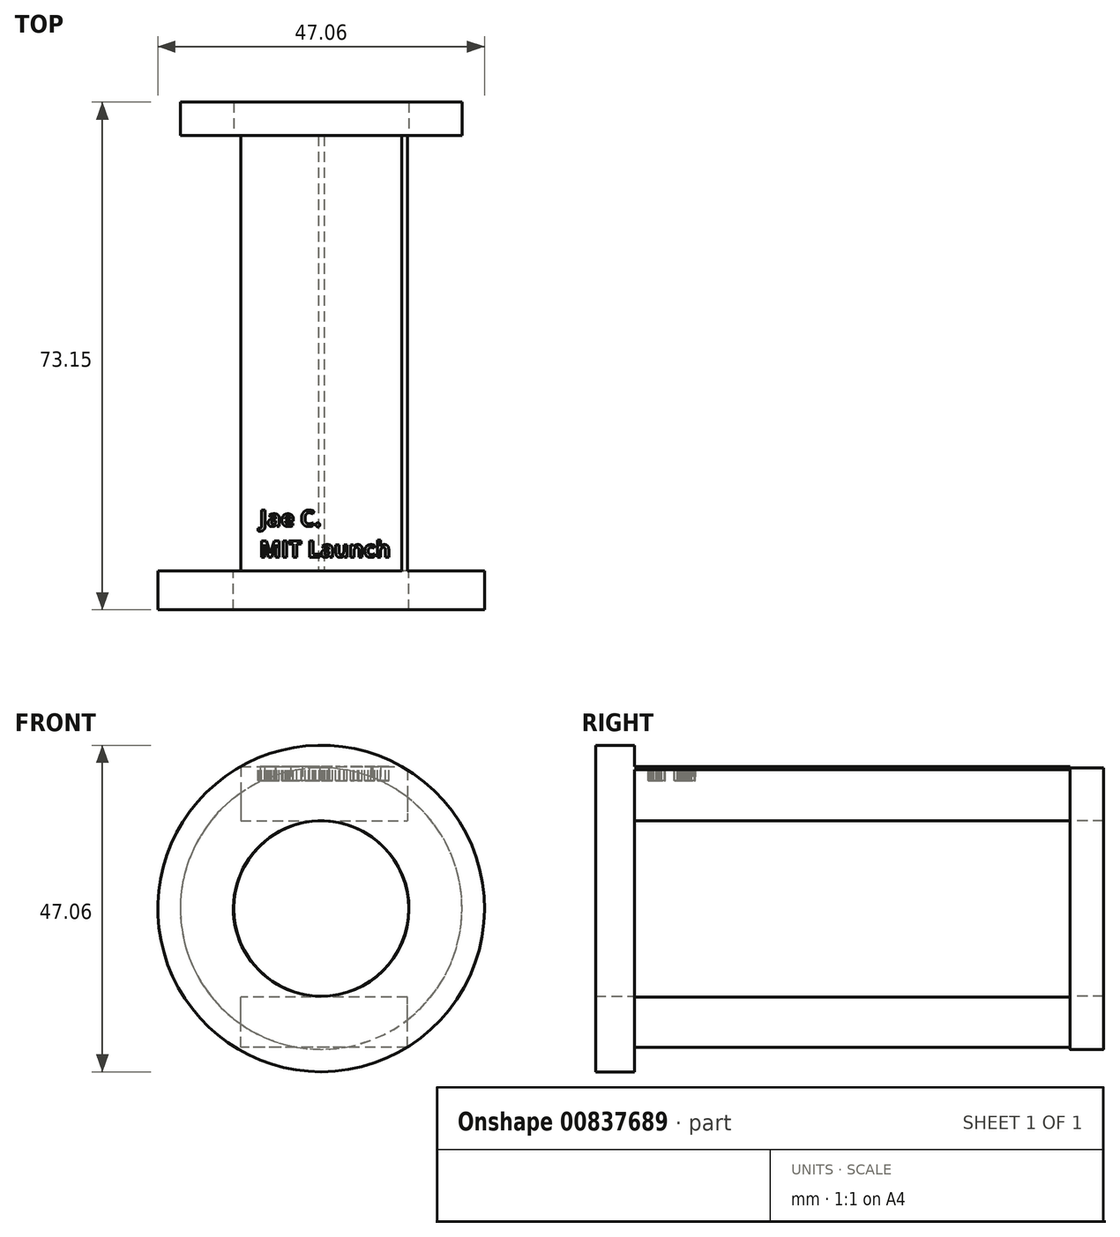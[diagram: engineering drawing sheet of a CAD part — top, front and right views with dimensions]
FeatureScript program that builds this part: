
annotation { "Feature Type Name" : "Feature", "Feature Type Description" : "" }
export const myFeature = defineFeature(function(context is Context, id is Id, definition is map)
    precondition{}
    {
        {
            var Q0;
            Q0=qCreatedBy(makeId("Front.planeOp"),FACE);
            var sketch = newSketch(context, id + "F0", { "sketchPlane" : qUnion([Q0])});
            skCircle(sketch, "E0", {"center": v(0, 0) * mm, "radius": 12.65 * mm});
            skCircle(sketch, "E1", {"center": v(0, 0) * mm, "radius": 23.53 * mm});
            skSolve(sketch);
        }
        {
            var Q0;
            Q0 = qSketchRegion(id + "F0", true);
            extrude(context, id + "F1", {"entities" : qUnion([Q0]), "depth" : 5.6 * mm, "offsetDistance" : 25.4 * mm});
        }
        {
            var Q0;
            Q0=makeQuery(id+"F1.opExtrude","CAP_FACE",FACE,{"disambiguationData":[OSD([sQuery(id+"F0.wireOp",EDGE,"E0"),sQuery(id+"F0.wireOp",EDGE,"E1")])],"isStart":true});
            var sketch = newSketch(context, id + "F2", { "sketchPlane" : qUnion([Q0])});
            skLineSegment(sketch, "E2.bottom", {"start": v(11.6, 20.47) * mm, "end": v(-12.41, 20.47) * mm});
            skLineSegment(sketch, "E2.top", {"start": v(11.6, 12.64) * mm, "end": v(-12.41, 12.64) * mm});
            skLineSegment(sketch, "E2.left", {"start": v(11.6, 20.47) * mm, "end": v(11.6, 12.64) * mm});
            skLineSegment(sketch, "E2.right", {"start": v(-12.41, 20.47) * mm, "end": v(-12.41, 12.64) * mm});
            skLineSegment(sketch, "E3.bottom", {"start": v(-12.41, -19.99) * mm, "end": v(11.6, -19.99) * mm});
            skLineSegment(sketch, "E3.top", {"start": v(-12.41, -12.76) * mm, "end": v(11.6, -12.76) * mm});
            skLineSegment(sketch, "E3.left", {"start": v(-12.41, -19.99) * mm, "end": v(-12.41, -12.76) * mm});
            skLineSegment(sketch, "E3.right", {"start": v(11.6, -19.99) * mm, "end": v(11.6, -12.76) * mm});
            skSolve(sketch);
        }
        {
            var Q0;
            {var subQ9=sQuery(id+"F2.wireOp",EDGE,"E2.left");Q0=makeQuery(id+"F2.imprint","IMPRINT",FACE,{"disambiguationData":[TD([[makeQuery(id+"F2.imprint","IMPRINT",EDGE,{"derivedFrom":subQ9}),-1.0]])]});}
            var Q1;
            Q1=makeQuery(id+"F2.imprint","IMPRINT",FACE,{"disambiguationData":[TD([[makeQuery(id+"F2.imprint","IMPRINT",EDGE,{"derivedFrom":sQuery(id+"F2.wireOp",EDGE,"E3.bottom")}),1.0]])]});
            extrude(context, id + "F3", {"entities" : qUnion([Q0, Q1]), "operationType" : NewBodyOperationType.ADD, "depth" : 62.74 * mm, "offsetDistance" : 25.4 * mm});
        }
        {
            var Q0;
            Q0=makeQuery(id+"F3.opExtrude","CAP_FACE",FACE,{"disambiguationData":[OSD([sQuery(id+"F0.wireOp",EDGE,"E0"),sQuery(id+"F0.wireOp",EDGE,"E1"),sQuery(id+"F2.wireOp",EDGE,"E2.bottom"),sQuery(id+"F2.wireOp",EDGE,"E2.top"),sQuery(id+"F2.wireOp",EDGE,"E2.left"),sQuery(id+"F2.wireOp",EDGE,"E2.right")])],"isStart":false});
            var sketch = newSketch(context, id + "F4", { "sketchPlane" : qUnion([Q0])});
            skCircle(sketch, "E4", {"center": v(0, 0) * mm, "radius": 12.61 * mm});
            skCircle(sketch, "E5", {"center": v(0, 0) * mm, "radius": 20.29 * mm});
            skSolve(sketch);
        }
        {
            var Q0;
            Q0 = qSketchRegion(id + "F4", true);
            extrude(context, id + "F5", {"entities" : qUnion([Q0]), "operationType" : NewBodyOperationType.ADD, "depth" : 4.83 * mm, "offsetDistance" : 25.4 * mm});
        }
        {
            var Q0;
            Q0=makeQuery(id+"F3.opExtrude","SWEPT_FACE",FACE,{"disambiguationData":[OSD([sQuery(id+"F2.wireOp",EDGE,"E2.bottom")])]});
            var sketch = newSketch(context, id + "F6", { "sketchPlane" : qUnion([Q0])});
            skText(sketch, "E6", { "text": "Jae C.\nMIT Launch", "fontName": "OpenSans-Bold.ttf"});
            const initialGuessF6  = {"E6": [-0.00885, 0.00644, 1, 0, 0.00235]};
            skSetInitialGuess(sketch, initialGuessF6);
            skSolve(sketch);
        }
        {
            var Q0;
            Q0 = qSketchRegion(id + "F6", true);
            extrude(context, id + "F7", {"entities" : qUnion([Q0]), "operationType" : NewBodyOperationType.REMOVE, "oppositeDirection" : true, "depth" : 2.03 * mm, "offsetDistance" : 25.4 * mm});
        }
    });
